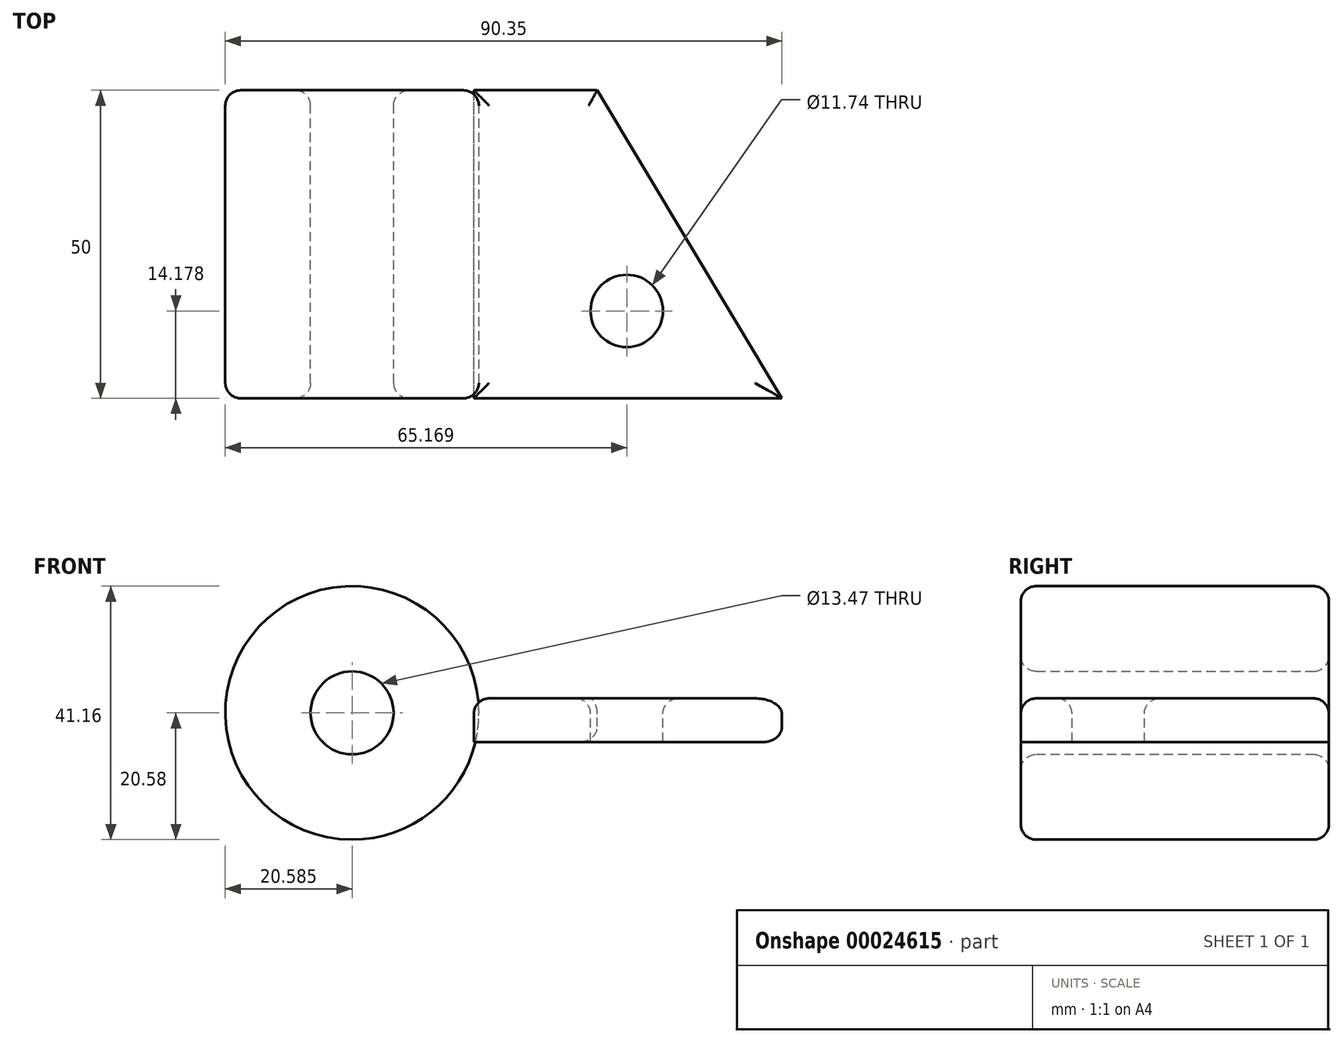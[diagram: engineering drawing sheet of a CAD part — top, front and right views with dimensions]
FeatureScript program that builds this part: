
annotation { "Feature Type Name" : "Feature", "Feature Type Description" : "" }
export const myFeature = defineFeature(function(context is Context, id is Id, definition is map)
    precondition{}
    {
        {
            var Q0;
            Q0=qCreatedBy(makeId("Front.planeOp"),FACE);
            var sketch = newSketch(context, id + "F0", { "sketchPlane" : qUnion([Q0])});
            skCircle(sketch, "E0", {"center": v(-44.76, 6.82) * mm, "radius": 20.58 * mm});
            skCircle(sketch, "E1", {"center": v(-44.76, 6.82) * mm, "radius": 6.74 * mm});
            skSolve(sketch);
        }
        {
            var Q0;
            Q0=makeQuery(id+"F0.imprint","IMPRINT",FACE,{"disambiguationData":[TD([[makeQuery(id+"F0.imprint","IMPRINT",EDGE,{"derivedFrom":sQuery(id+"F0.wireOp",EDGE,"E0")}),1.0]])]});
            extrude(context, id + "F1", {"entities" : qUnion([Q0]), "depth" : 50 * mm});
        }
        {
            var Q0;
            Q0=qCreatedBy(makeId("Right.planeOp"),FACE);
            var sketch = newSketch(context, id + "F2", { "sketchPlane" : qUnion([Q0])});
            skLineSegment(sketch, "E2.bottom", {"start": v(-50.14, 9.18) * mm, "end": v(0, 9.18) * mm});
            skLineSegment(sketch, "E2.top", {"start": v(-50.14, 2.1) * mm, "end": v(0, 2.1) * mm});
            skLineSegment(sketch, "E2.left", {"start": v(-50.14, 9.18) * mm, "end": v(-50.14, 2.1) * mm});
            skLineSegment(sketch, "E2.right", {"start": v(0, 9.18) * mm, "end": v(0, 2.1) * mm});
            skSolve(sketch);
        }
        {
            var Q0;
            Q0=makeQuery(id+"F2.imprint","IMPRINT",FACE,{"disambiguationData":[TD([[makeQuery(id+"F2.imprint","IMPRINT",EDGE,{"derivedFrom":sQuery(id+"F2.wireOp",EDGE,"E2.bottom")}),-1.0]])]});
            extrude(context, id + "F3", {"entities" : qUnion([Q0]), "oppositeDirection" : true, "depth" : 25 * mm});
        }
        {
            var Q0;
            Q0=makeQuery(id+"F3.opExtrude","CAP_FACE",FACE,{"disambiguationData":[OSD([sQuery(id+"F2.wireOp",EDGE,"E2.bottom"),sQuery(id+"F2.wireOp",EDGE,"E2.top"),sQuery(id+"F2.wireOp",EDGE,"E2.left"),sQuery(id+"F2.wireOp",EDGE,"E2.right")])],"isStart":true});
            extrude(context, id + "F4", {"entities" : qUnion([Q0]), "operationType" : NewBodyOperationType.ADD, "depth" : 25 * mm});
        }
        {
            var Q0;
            {var subQ0=sQuery(id+"F2.wireOp",EDGE,"E2.left");Q0=makeQuery(id+"F4.boolean.opBoolean","MERGE",FACE,{"derivedFrom":[makeQuery(id+"F3.opExtrude","SWEPT_FACE",FACE,{"disambiguationData":[OSD([subQ0])]}),makeQuery(id+"F4.opExtrude","SWEPT_FACE",FACE,{"disambiguationData":[OSD([subQ0])]})]});}
            var Q1;
            Q1=makeQuery(id+"F1.opExtrude","CAP_FACE",FACE,{"disambiguationData":[OSD([sQuery(id+"F0.wireOp",EDGE,"E0"),sQuery(id+"F0.wireOp",EDGE,"E1")])],"isStart":false});
            extrude(context, id + "F5", {"entities" : qUnion([Q0]), "operationType" : NewBodyOperationType.REMOVE, "endBound" : BoundingType.UP_TO_SURFACE, "oppositeDirection" : true, "endBoundEntityFace" : qUnion([Q1]), "depth" : 25 * mm});
        }
        {
            var Q0;
            {var subQ0=sQuery(id+"F2.wireOp",EDGE,"E2.bottom");Q0=makeQuery(id+"F4.boolean.opBoolean","MERGE",FACE,{"derivedFrom":[makeQuery(id+"F3.opExtrude","SWEPT_FACE",FACE,{"disambiguationData":[OSD([subQ0])]}),makeQuery(id+"F4.opExtrude","SWEPT_FACE",FACE,{"disambiguationData":[OSD([subQ0])]})]});}
            var sketch = newSketch(context, id + "F6", { "sketchPlane" : qUnion([Q0])});
            skLineSegment(sketch, "E3", {"start": v(25, -50) * mm, "end": v(-4.96, 0) * mm});
            skSolve(sketch);
        }
        {
            var Q0;
            {var subQ3=sQuery(id+"F6.wireOp",EDGE,"E3");Q0=makeQuery(id+"F6.imprint","IMPRINT",FACE,{"disambiguationData":[TD([[makeQuery(id+"F6.imprint","IMPRINT",EDGE,{"derivedFrom":subQ3}),-1.0]])]});}
            extrude(context, id + "F7", {"entities" : qUnion([Q0]), "operationType" : NewBodyOperationType.REMOVE, "endBound" : BoundingType.THROUGH_ALL, "oppositeDirection" : true, "depth" : 25 * mm});
        }
        {
            var Q0;
            {var subQ0=sQuery(id+"F2.wireOp",EDGE,"E2.bottom");Q0=makeQuery(id+"F4.boolean.opBoolean","MERGE",FACE,{"derivedFrom":[makeQuery(id+"F3.opExtrude","SWEPT_FACE",FACE,{"disambiguationData":[OSD([subQ0])]}),makeQuery(id+"F4.opExtrude","SWEPT_FACE",FACE,{"disambiguationData":[OSD([subQ0])]})]});}
            var sketch = newSketch(context, id + "F8", { "sketchPlane" : qUnion([Q0])});
            skCircle(sketch, "E4", {"center": v(-0.18, -35.82) * mm, "radius": 5.87 * mm});
            skSolve(sketch);
        }
        {
            var Q0;
            Q0=makeQuery(id+"F8.imprint","IMPRINT",FACE,{"disambiguationData":[TD([[makeQuery(id+"F8.imprint","IMPRINT",EDGE,{"derivedFrom":sQuery(id+"F8.wireOp",EDGE,"E4")}),1.0]])]});
            extrude(context, id + "F9", {"entities" : qUnion([Q0]), "operationType" : NewBodyOperationType.REMOVE, "endBound" : BoundingType.THROUGH_ALL, "oppositeDirection" : true, "depth" : 25 * mm});
        }
        {
            var Q0;
            Q0=makeQuery(id+"F1.opExtrude","CAP_EDGE",EDGE,{"disambiguationData":[OSD([sQuery(id+"F0.wireOp",EDGE,"E0")])],"isStart":false});
            var Q1;
            Q1=makeQuery(id+"F5.boolean.opBoolean","COPY",EDGE,{"derivedFrom":makeQuery(id+"F5.opExtrude","CAP_EDGE",EDGE,{"disambiguationData":[OSD([sQuery(id+"F2.wireOp",EDGE,"E2.bottom"),sQuery(id+"F2.wireOp",EDGE,"E2.left")])],"isStart":false})});
            var Q2;
            Q2=makeQuery(id+"F5.boolean.opBoolean","COPY",EDGE,{"derivedFrom":makeQuery(id+"F5.opExtrude","CAP_EDGE",EDGE,{"disambiguationData":[OSD([sQuery(id+"F2.wireOp",EDGE,"E2.top"),sQuery(id+"F2.wireOp",EDGE,"E2.left")])],"isStart":false})});
            var Q3;
            {var subQ0=sQuery(id+"F2.wireOp",EDGE,"E2.bottom");Q3=makeQuery(id+"F4.boolean.opBoolean","MERGE",FACE,{"derivedFrom":[makeQuery(id+"F3.opExtrude","SWEPT_FACE",FACE,{"disambiguationData":[OSD([subQ0])]}),makeQuery(id+"F4.opExtrude","SWEPT_FACE",FACE,{"disambiguationData":[OSD([subQ0])]})]});}
            var Q4;
            Q4=makeQuery(id+"F1.opExtrude","SWEPT_FACE",FACE,{"disambiguationData":[OSD([sQuery(id+"F0.wireOp",EDGE,"E0")])]});
            var Q5;
            {var subQ0=sQuery(id+"F2.wireOp",EDGE,"E2.top");Q5=makeQuery(id+"F7.boolean.opBoolean","INTERSECT",EDGE,{"derivedFrom":[makeQuery(id+"F4.boolean.opBoolean","MERGE",FACE,{"derivedFrom":[makeQuery(id+"F3.opExtrude","SWEPT_FACE",FACE,{"disambiguationData":[OSD([subQ0])]}),makeQuery(id+"F4.opExtrude","SWEPT_FACE",FACE,{"disambiguationData":[OSD([subQ0])]})]}),makeQuery(id+"F7.opExtrude","SWEPT_FACE",FACE,{"disambiguationData":[OSD([sQuery(id+"F6.wireOp",EDGE,"E3")])]})]});}
            fillet(context, id + "F10", {"entities" : qUnion([Q0, Q1, Q2, Q3, Q4, Q5]), "radius" : 2.5 * mm, "tangentPropagation" : true, "allowEdgeOverflow" : false});
        }
        {
            var Q0;
            Q0=makeQuery(id+"F1.opExtrude","CAP_EDGE",EDGE,{"disambiguationData":[OSD([sQuery(id+"F0.wireOp",EDGE,"E1")])],"isStart":true});
            var Q1;
            Q1=makeQuery(id+"F1.opExtrude","CAP_EDGE",EDGE,{"disambiguationData":[OSD([sQuery(id+"F0.wireOp",EDGE,"E1")])],"isStart":false});
            fillet(context, id + "F11", {"entities" : qUnion([Q0, Q1]), "radius" : 2.5 * mm, "tangentPropagation" : true, "allowEdgeOverflow" : false});
        }
    });
